# Revit family: 0030445
name_source: partatom
category: Lighting Fixtures
revit_build: Autodesk Revit 2017 (Build: 20190507_1515(x64)
units: mm (PartAtom-declared; Revit-internal decimal feet)

## family parameters
Cut with Voids When Loaded = No
Host = Face
Light Source = Yes
OmniClass Number = 23.80.70.00
OmniClass Title = Lighting
Part Type = Normal
Room Calculation Point = No
Round Connector Dimension = Use Diameter
Shared = No

## types (4) — shared parameters
Assembly Code = D5020200
AssetType = Fixed
ClassificationName = Uniclass2015
ClassificationValue = EF_70_80
Color Filter = 16777215
Default Elevation = 1219 mm
Dimming Lamp Color Temperature Shift = <None>
DocumentationLiterature = http://www.sylvania-lighting.com
ElectricShockClassification = Class II
Emit Shape Visible in Rendering = No
Emit from Circle Diameter = 610 mm
HEIGHT_SYL = 94 mm
IfcExportAs = IfcLightFixtureType
IfcExportType = IfcLightFixtureType
ImpactProtectionIndex = IK07
IngressProtection = IP20
Keynote = 16500
LUM_CHAMFER_SYL = 4 mm  [stored 0.0131234 ft]
Lamp = LED
LampColourRenderingIndex = 80
LampMacAdamStep = 5
LampsType = LED
Manufacturer = Feilo Sylvania
ManufacturerName = Feilo Sylvania
Material = aluminium housing, pc polycarbonate diffuser
Material_1_SYL = Default
Material_2_SYL = <By Category>
Material_3_SYL = <By Category>
Material_4_SYL = <By Category>
NominalHeight = 95 mm
PLATE_THICKNESS_SYL = 2 mm  [stored 0.00656168 ft]
PowerFactor = 0.9
Tilt Angle = -90.00°
Type Image = <None>
URL = http://www.sylvania-lighting.com
Voltage = 0 V
zero-valued in all types: Cost

## per-type parameters (varying)
| type | 0_M_SYL | 0_S_SYL | Apparent Load | BOTTOM_RAD2_SYL | BOTTOM_RAD_SYL | DIF_RAD_SYL | Description | LUM_H_SYL | LUM_RAD_SYL | LampColourTemperature | LampNominalLuminous | LuminousEfficacy | Model | ModelNumber | ModelReference | Name | NominalDepth | NominalLength | Photometric Web File | PowerConsumption | TOP_RAD_SYL | TypeName | Weight |
| 0030447 ST DOWNLIGHT 220 2025LM 840 SURFACE | Yes | No | 21 VA | 108 mm | 110 mm | 88 mm | Surface mounted LED downlight with diameter size of 220mm. Ideal replacement for 1x42W CFL downlights. The polycarbonate diffuser allows for a wider light distribution and increased spacings between luminiares. Loop in loop out connector allows for quick installation. Die-cast aluminium body, 2025LM, 21W, 101lm/W, 4000K, Driver Current: 600mA, CRI80, Non-dimmable LED driver, IP20, IK07, 50,000 hrs (L70), (HxW) 94x220mm, Class 2,  220-240V, energy class: A++, A+, A | 54 mm | 53 mm | 4000 K | 2025 lm | 96 lm/W | START Downlight 220 2025lm 840 Surface | 0030447 | START Downlight 220 2025lm 840 Surface | START Downlight 220 2025lm 840 Surface | 220 mm | 220 mm | 0030447.ies | 21 W | 107 mm | START Downlight 220 2025lm 840 Surface | 6.416 kg |
| 0030446 ST DOWNLIGHT 220 1950LM 830 SURFACE | Yes | No | 21 VA | 108 mm | 110 mm | 88 mm | Surface mounted LED downlight with diameter size of 220mm. Ideal replacement for 1x42W CFL downlights. The polycarbonate diffuser allows for a wider light distribution and increased spacings between luminiares. Loop in loop out connector allows for quick installation. Die-cast aluminium body, 1950LM, 21W, 98lm/W, 3000K, Driver Current: 600mA, CRI80, Non-dimmable LED driver, IP20, IK07, 50,000 hrs (L70), (HxW) 94x220mm, Class 2,  220-240V, energy class: A++, A+, A | 54 mm | 53 mm | 3000 K | 1950 lm | 93 lm/W | START Downlight 220 1950lm 830 Surface | 0030446 | START Downlight 220 1950lm 830 Surface | START Downlight 220 1950lm 830 Surface | 220 mm | 220 mm | 0030446.ies | 21 W | 107 mm | START Downlight 220 1950lm 830 Surface | 6.416 kg |
| 0030445 ST DOWNLIGHT 165 1175LM 840 SURFACE | No | Yes | 12 VA | 80 mm | 82 mm | 60 mm  [stored 0.19685 ft] | Surface mounted LED downlight with diameter size of 165mm. Ideal replacement for 1x26W CFL downlights. The polycarbonate diffuser allows for a wider light distribution and increased spacings between luminiares. Loop in loop out connector allows for quick installation. Die-cast aluminium body, 1175LM, 12W, 98lm/W, 4000K, Driver Current: 290mA, CRI80, Non-dimmable LED driver, IP20, IK07, 50,000 hrs (L70), (HxW) 94x165mm, Class 2,  220-240V, energy class: A++, A+, A | 42 mm  [stored 0.137795 ft] | 40 mm  [stored 0.131234 ft] | 4000 K | 1175 lm | 98 lm/W | START Downlight 165 1175lm 840 Surface | 0030445 | START Downlight 165 1175lm 840 Surface | START Downlight 165 1175lm 840 Surface | 165 mm | 165 mm | 0030445.ies | 12 W | 79 mm | START Downlight 165 1175lm 840 Surface | 7.02 kg |
| 0030444 ST DOWNLIGHT 165 1100LM 830 SURFACE | No | Yes | 12 VA | 80 mm | 82 mm | 60 mm  [stored 0.19685 ft] | Surface mounted LED downlight with diameter size of 165mm. Ideal replacement for 1x26W CFL downlights. The polycarbonate diffuser allows for a wider light distribution and increased spacings between luminiares. Loop in loop out connector allows for quick installation. Die-cast aluminium body, 1100LM, 12W, 92lm/W, 3000K, Driver Current: 290mA, CRI80, Non-dimmable LED driver, IP20, IK07, 50,000 hrs (L70), (HxW) 94x165mm, Class 2,  220-240V, energy class: A++, A+, A | 42 mm  [stored 0.137795 ft] | 40 mm  [stored 0.131234 ft] | 3000 K | 1100 lm | 92 lm/W | START Downlight 165 1100lm 830 Surface | 0030444 | START Downlight 165 1100lm 830 Surface | START Downlight 165 1100lm 830 Surface | 165 mm | 165 mm | 0030444.ies | 12 W | 79 mm | START Downlight 165 1100lm 830 Surface | 7.02 kg |

note: [stored X ft] marks values corroborated as IEEE doubles in the binary element streams (Revit-internal decimal feet)

## geometry (parser evidence)
native form markers: Sweep x2
no freeform markers — native parametric forms only
